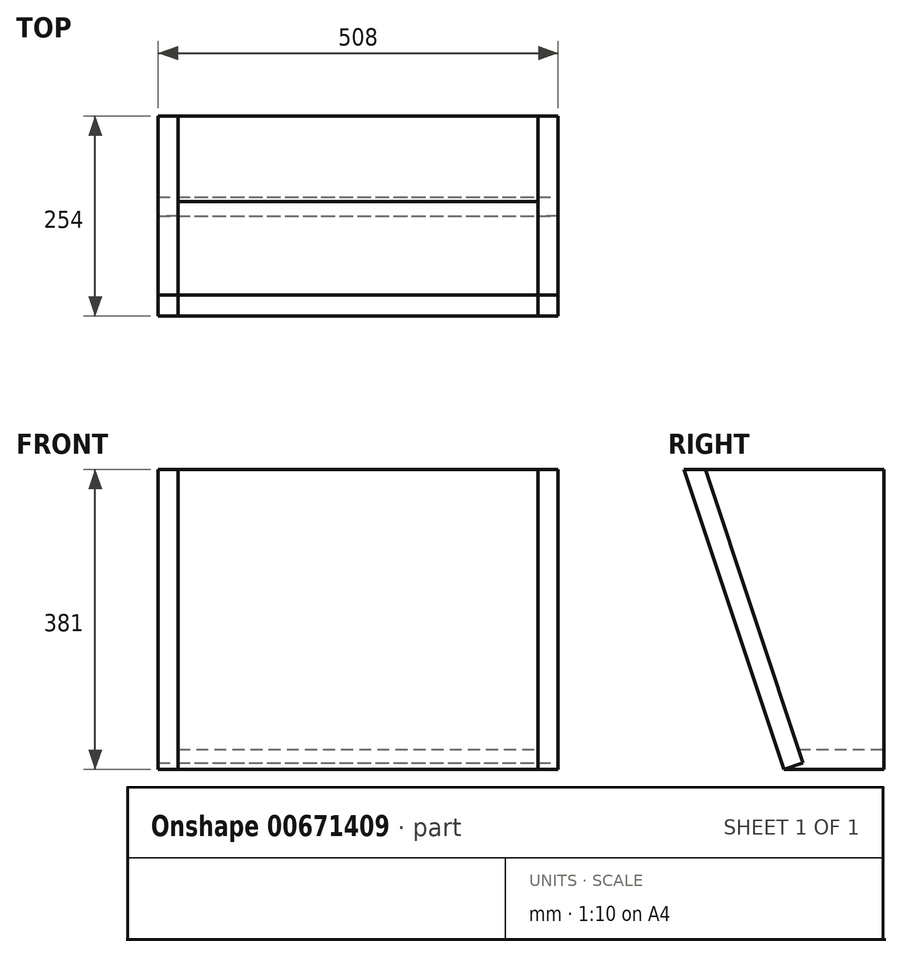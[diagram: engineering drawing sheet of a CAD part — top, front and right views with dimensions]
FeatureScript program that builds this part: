
annotation { "Feature Type Name" : "Feature", "Feature Type Description" : "" }
export const myFeature = defineFeature(function(context is Context, id is Id, definition is map)
    precondition{}
    {
        {
            var Q0;
            Q0=qCreatedBy(makeId("Front.planeOp"),FACE);
            var sketch = newSketch(context, id + "F0", { "sketchPlane" : qUnion([Q0])});
            skLineSegment(sketch, "E0.bottom", {"start": v(-254, 190.5) * mm, "end": v(254, 190.5) * mm});
            skLineSegment(sketch, "E0.top", {"start": v(-254, -190.5) * mm, "end": v(254, -190.5) * mm});
            skLineSegment(sketch, "E0.left", {"start": v(-254, 190.5) * mm, "end": v(-254, -190.5) * mm});
            skLineSegment(sketch, "E0.right", {"start": v(254, 190.5) * mm, "end": v(254, -190.5) * mm});
            skPoint(sketch, "E0.middle", {"position": v(0, 0) * mm});
            skSolve(sketch);
        }
        {
            var Q0;
            Q0=makeQuery(id+"F0.imprint","IMPRINT",FACE,{"disambiguationData":[TD([[makeQuery(id+"F0.imprint","IMPRINT",EDGE,{"derivedFrom":sQuery(id+"F0.wireOp",EDGE,"E0.bottom")}),-1.0]])]});
            var sketch = newSketch(context, id + "F1", { "sketchPlane" : qUnion([Q0])});
            skLineSegment(sketch, "E1.0", {"start": v(-254, 190.5) * mm, "end": v(-228.6, 190.5) * mm});
            skLineSegment(sketch, "E1.1", {"start": v(-254, 190.5) * mm, "end": v(-254, -190.5) * mm});
            skLineSegment(sketch, "E1.2", {"start": v(254, 190.5) * mm, "end": v(254, -190.5) * mm});
            skLineSegment(sketch, "E1.3", {"start": v(-254, -190.5) * mm, "end": v(-228.6, -190.5) * mm});
            skLineSegment(sketch, "E2", {"start": v(-228.6, 190.5) * mm, "end": v(-228.6, -190.5) * mm});
            skLineSegment(sketch, "E3", {"start": v(228.6, 190.5) * mm, "end": v(228.6, -190.5) * mm});
            skLineSegment(sketch, "E4.trimOffspring", {"start": v(228.6, 190.5) * mm, "end": v(254, 190.5) * mm});
            skLineSegment(sketch, "E5.trimOffspring", {"start": v(228.6, -190.5) * mm, "end": v(254, -190.5) * mm});
            skSolve(sketch);
        }
        {
            var Q0;
            Q0 = qSketchRegion(id + "F1", true);
            extrude(context, id + "F2", {"entities" : qUnion([Q0]), "depth" : 254 * mm, "offsetDistance" : 25.4 * mm});
        }
        {
            var Q0;
            Q0=makeQuery(id+"F2.opExtrude","SWEPT_FACE",FACE,{"disambiguationData":[OSD([sQuery(id+"F1.wireOp",EDGE,"E1.1")])]});
            var sketch = newSketch(context, id + "F3", { "sketchPlane" : qUnion([Q0])});
            skPoint(sketch, "E6.0", {"position": v(254, 190.5) * mm});
            skLineSegment(sketch, "E6.1", {"start": v(254, -190.5) * mm, "end": v(127, -190.5) * mm});
            skLineSegment(sketch, "E7", {"start": v(254, 190.5) * mm, "end": v(127, -190.5) * mm});
            skPoint(sketch, "E8.orphan", {"position": v(0, -190.5) * mm});
            skSolve(sketch);
        }
        {
            var Q0;
            Q0=makeQuery(id+"F3.imprint","IMPRINT",FACE,{"disambiguationData":[TD([[makeQuery(id+"F3.imprint","IMPRINT",EDGE,{"derivedFrom":sQuery(id+"F3.wireOp",EDGE,"E6.1")}),-1.0]])]});
            extrude(context, id + "F4", {"entities" : qUnion([Q0]), "operationType" : NewBodyOperationType.REMOVE, "oppositeDirection" : true, "depth" : 635 * mm, "offsetDistance" : 25.4 * mm});
        }
        {
            var Q0;
            Q0=makeQuery(id+"F4.boolean.opBoolean","COPY",FACE,{"disambiguationData":[TD([makeQuery(id+"F2.opExtrude","SWEPT_FACE",FACE,{"disambiguationData":[OSD([sQuery(id+"F1.wireOp",EDGE,"E1.2")])]})])],"derivedFrom":makeQuery(id+"F4.opExtrude","SWEPT_FACE",FACE,{"disambiguationData":[OSD([sQuery(id+"F3.wireOp",EDGE,"E7")])]})});
            var sketch = newSketch(context, id + "F5", { "sketchPlane" : qUnion([Q0])});
            skPoint(sketch, "E9.0", {"position": v(-254, 180.72) * mm});
            skPoint(sketch, "E9.1", {"position": v(254, -180.72) * mm});
            skPoint(sketch, "E10.0", {"position": v(-254, 261.05) * mm});
            skPoint(sketch, "E11.0", {"position": v(254, -140.56) * mm});
            skLineSegment(sketch, "E12.bottom", {"start": v(-254, 261.05) * mm, "end": v(254, 261.05) * mm});
            skLineSegment(sketch, "E12.top", {"start": v(-254, -140.56) * mm, "end": v(254, -140.56) * mm});
            skLineSegment(sketch, "E12.left", {"start": v(-254, 261.05) * mm, "end": v(-254, -140.56) * mm});
            skLineSegment(sketch, "E12.right", {"start": v(254, 261.05) * mm, "end": v(254, -140.56) * mm});
            skSolve(sketch);
        }
        {
            var Q0;
            Q0 = qSketchRegion(id + "F5", true);
            extrude(context, id + "F6", {"entities" : qUnion([Q0]), "oppositeDirection" : true, "depth" : 25.4 * mm, "offsetDistance" : 25.4 * mm});
        }
        {
            var Q0;
            Q0=makeQuery(id+"F6.opExtrude","SWEPT_FACE",FACE,{"disambiguationData":[OSD([sQuery(id+"F5.wireOp",EDGE,"E12.right")])]});
            var sketch = newSketch(context, id + "F7", { "sketchPlane" : qUnion([Q0])});
            skLineSegment(sketch, "E13.1", {"start": v(-229.9, 198.53) * mm, "end": v(-254, 190.5) * mm});
            skPoint(sketch, "E13.3", {"position": v(-241.95, 194.52) * mm});
            skPoint(sketch, "E14.orphan", {"position": v(-102.9, -182.47) * mm});
            skPoint(sketch, "E13.2.end.orphan", {"position": v(0, 190.5) * mm});
            skPoint(sketch, "E13.2.start.orphan", {"position": v(-254, 190.5) * mm});
            skLineSegment(sketch, "E15.0", {"start": v(-102.9, -182.47) * mm, "end": v(-229.9, 198.53) * mm});
            skLineSegment(sketch, "E16.0", {"start": v(-254, 190.5) * mm, "end": v(0, 190.5) * mm});
            skSolve(sketch);
        }
        {
            var Q0;
            Q0=makeQuery(id+"F2.opExtrude","SWEPT_FACE",FACE,{"disambiguationData":[OSD([sQuery(id+"F1.wireOp",EDGE,"E3")])]});
            var sketch = newSketch(context, id + "F8", { "sketchPlane" : qUnion([Q0])});
            skLineSegment(sketch, "E17.0.0", {"start": v(127, -190.5) * mm, "end": v(254, 190.5) * mm});
            skLineSegment(sketch, "E17.0.1", {"start": v(254, 190.5) * mm, "end": v(229.9, 198.53) * mm});
            skLineSegment(sketch, "E17.0.2", {"start": v(229.9, 198.53) * mm, "end": v(102.9, -182.47) * mm});
            skLineSegment(sketch, "E17.0.3", {"start": v(102.9, -182.47) * mm, "end": v(127, -190.5) * mm});
            skLineSegment(sketch, "E18", {"start": v(0, -165.1) * mm, "end": v(135.47, -165.1) * mm});
            skSolve(sketch);
        }
        {
            var Q0;
            {var subQ7=sQuery(id+"F8.wireOp",EDGE,"E17.0.3");Q0=makeQuery(id+"F8.imprint","IMPRINT",FACE,{"disambiguationData":[TD([[makeQuery(id+"F8.imprint","IMPRINT",EDGE,{"derivedFrom":subQ7}),-1.0]])]});}
            extrude(context, id + "F9", {"entities" : qUnion([Q0]), "endBound" : BoundingType.UP_TO_NEXT, "depth" : 25.4 * mm, "offsetDistance" : 25.4 * mm});
        }
        {
            var Q0;
            {var subQ0=sQuery(id+"F7.wireOp",EDGE,"E13.1");Q0=makeQuery(id+"F7.imprint","IMPRINT",FACE,{"disambiguationData":[TD([[makeQuery(id+"F7.imprint","IMPRINT",EDGE,{"derivedFrom":subQ0}),1.0]])]});}
            extrude(context, id + "F10", {"entities" : qUnion([Q0]), "operationType" : NewBodyOperationType.REMOVE, "endBound" : BoundingType.THROUGH_ALL, "oppositeDirection" : true, "depth" : 25.4 * mm, "offsetDistance" : 25.4 * mm});
        }
    });
